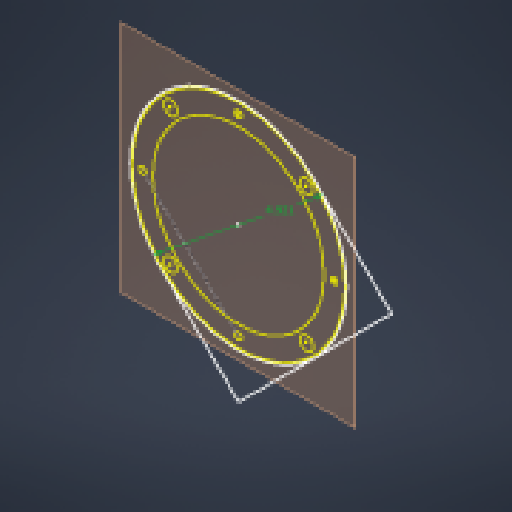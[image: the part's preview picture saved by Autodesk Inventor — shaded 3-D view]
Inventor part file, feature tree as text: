
AUTODESK INVENTOR PART (.ipt)
format: ipt  version: 2024 (Build 280153000, 153)  size: 139,776 bytes
history: native  units: in
note: dims shown in document units (in); Inventor stores cm internally (conversion verified against a paired STEP export)
features: other x3, plane x1, extrude x1, sketch x1, reference x1
ambient origin geometry x8: Origin, YZ Plane, XZ Plane, XY Plane, X Axis, Y Axis, Z Axis, Center Point
bodies: Solid1 (feature_tree)
feature tree (7):
  plane  "Work Plane1"
  extrude  "Extrusion1"  Depth=0.25in TaperAngle=0.0deg
  sketch  "Sketch1"  dims[d0=4.9213in d1=0.25in d2=0.0in]
  reference  "Reference1"
  other  "<userpath>\CodingProjects\C-AAM\CAD\V1\Parts\2ndAxis.iam"
  other  "2ndAxis.iam"
  other  "TopSpacer:1"
